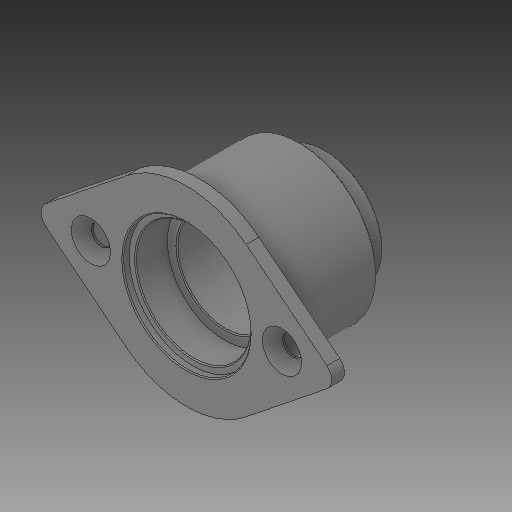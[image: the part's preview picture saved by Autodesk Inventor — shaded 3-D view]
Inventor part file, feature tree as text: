
AUTODESK INVENTOR PART (.ipt)
format: ipt  version: 2019 (Build 230136000, 136)  size: 167,936 bytes
history: native  units: in
note: dims shown in document units (in); Inventor stores cm internally (conversion verified against a paired STEP export)
features: chamfer x1
ambient origin geometry x8: Origin, YZ Plane, XZ Plane, XY Plane, X Axis, Y Axis, Z Axis, Center Point
bodies: Solid1 (feature_tree)
feature tree (1):
  chamfer  "Chamfer1"  [1 undecoded]
note: 1 required parameter value undecoded (feature->parameter linkage not recoverable at this tier; creation-order binding heuristic only, values carry confidence <= 0.55)
